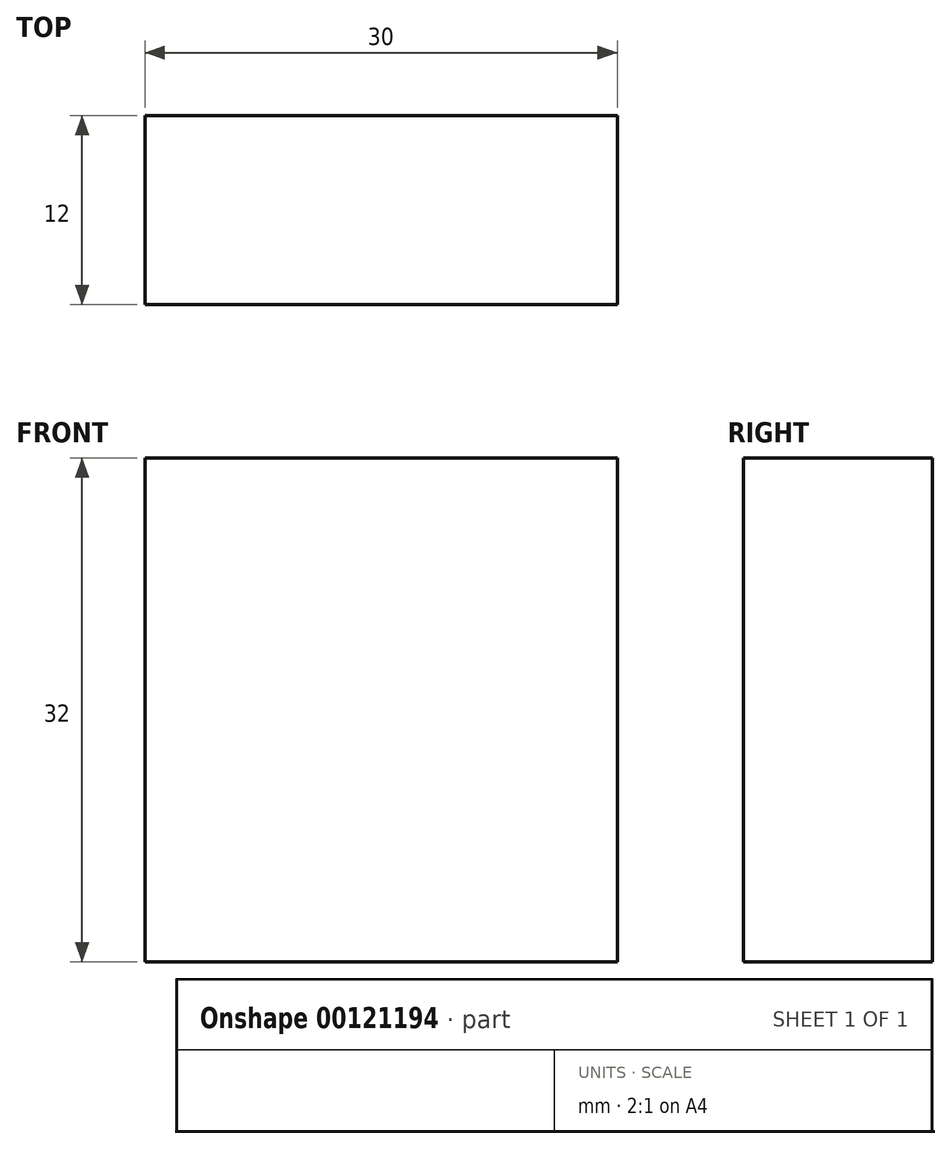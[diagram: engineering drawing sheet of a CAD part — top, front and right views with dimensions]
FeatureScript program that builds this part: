
annotation { "Feature Type Name" : "Feature", "Feature Type Description" : "" }
export const myFeature = defineFeature(function(context is Context, id is Id, definition is map)
    precondition{}
    {
        {
            var Q0;
            Q0=qCreatedBy(makeId("Front.planeOp"),FACE);
            var sketch = newSketch(context, id + "F0", { "sketchPlane" : qUnion([Q0])});
            skLineSegment(sketch, "E0.bottom", {"start": v(15, -16) * mm, "end": v(-15, -16) * mm});
            skLineSegment(sketch, "E0.top", {"start": v(15, 16) * mm, "end": v(-15, 16) * mm});
            skLineSegment(sketch, "E0.left", {"start": v(15, -16) * mm, "end": v(15, 16) * mm});
            skLineSegment(sketch, "E0.right", {"start": v(-15, -16) * mm, "end": v(-15, 16) * mm});
            skPoint(sketch, "E0.middle", {"position": v(0, 0) * mm});
            skSolve(sketch);
        }
        {
            var Q0;
            Q0=qSketchRegion(id+"F0",true);
            extrude(context, id + "F1", {"entities" : qUnion([Q0]), "depth" : 12 * mm});
        }
    });
